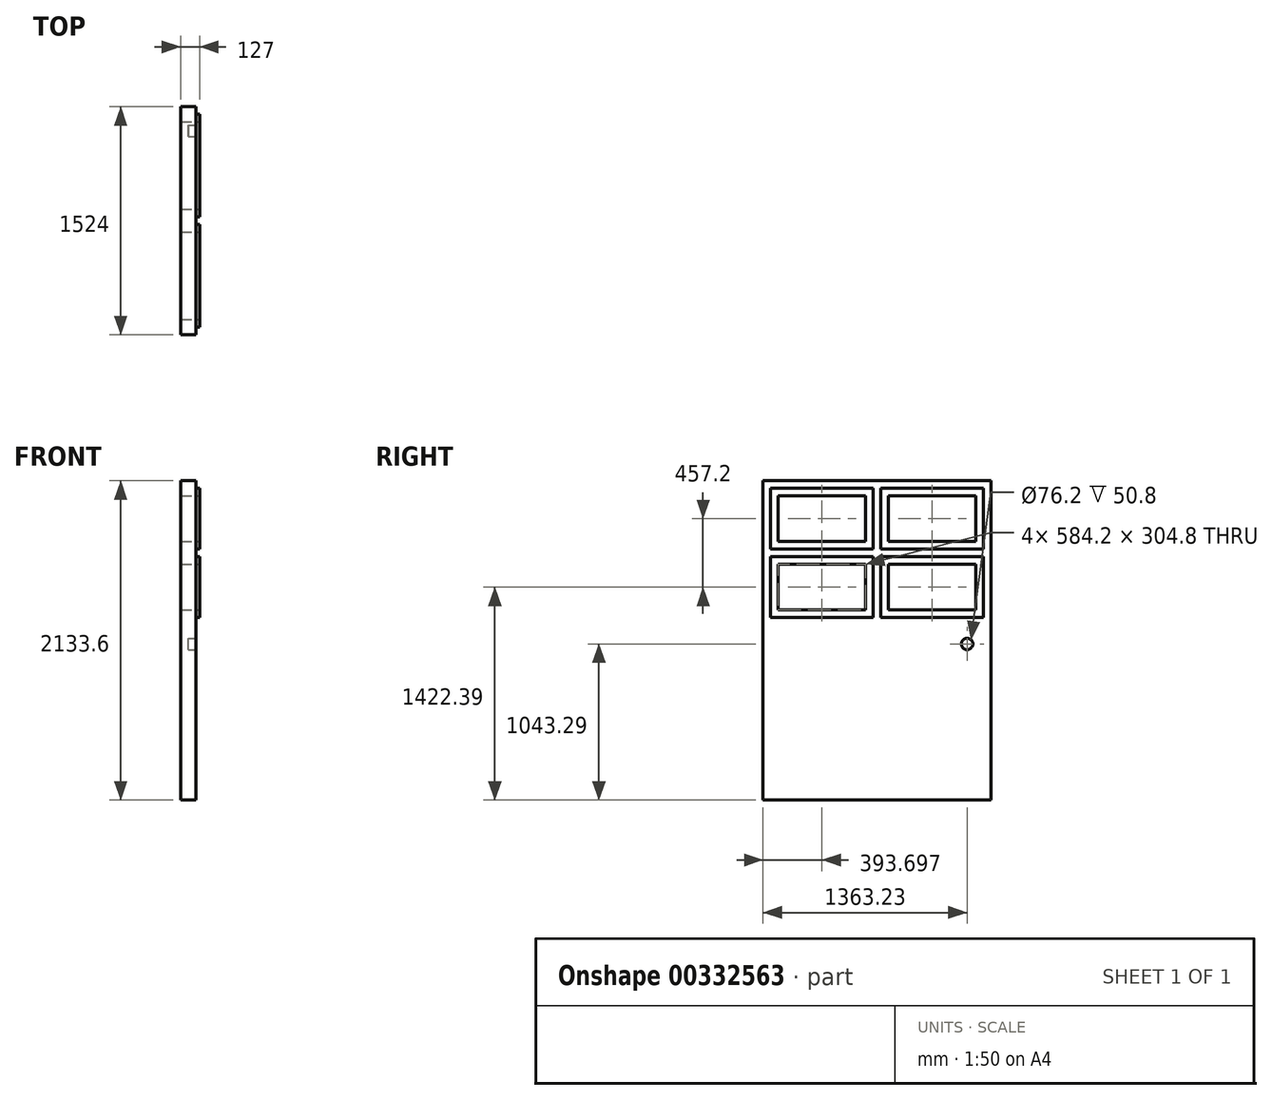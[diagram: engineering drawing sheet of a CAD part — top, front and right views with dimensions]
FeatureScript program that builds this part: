
annotation { "Feature Type Name" : "Feature", "Feature Type Description" : "" }
export const myFeature = defineFeature(function(context is Context, id is Id, definition is map)
    precondition{}
    {
        {
            var Q0;
            Q0=qCreatedBy(makeId("Right.planeOp"),FACE);
            var sketch = newSketch(context, id + "F0", { "sketchPlane" : qUnion([Q0])});
            skLineSegment(sketch, "E0.bottom", {"start": v(-1630.42, -5805.97) * mm, "end": v(-106.42, -5805.97) * mm});
            skLineSegment(sketch, "E0.top", {"start": v(-1630.42, -7939.57) * mm, "end": v(-106.42, -7939.57) * mm});
            skLineSegment(sketch, "E0.left", {"start": v(-1630.42, -5805.97) * mm, "end": v(-1630.42, -7939.57) * mm});
            skLineSegment(sketch, "E0.right", {"start": v(-106.42, -5805.97) * mm, "end": v(-106.42, -7939.57) * mm});
            skSolve(sketch);
        }
        {
            var Q0;
            Q0 = qSketchRegion(id + "F0", true);
            var Q1;
            Q1=makeQuery(id+"F0.imprint","IMPRINT",FACE,{"disambiguationData":[TD([[makeQuery(id+"F0.imprint","IMPRINT",EDGE,{"derivedFrom":sQuery(id+"F0.wireOp",EDGE,"E0.bottom")}),-1.0]])]});
            extrude(context, id + "F1", {"entities" : qUnion([Q0, Q1]), "depth" : 101.6 * mm});
        }
        {
            var Q0;
            Q0=makeQuery(id+"F1.opExtrude","CAP_FACE",FACE,{"disambiguationData":[OSD([sQuery(id+"F0.wireOp",EDGE,"E0.bottom"),sQuery(id+"F0.wireOp",EDGE,"E0.top"),sQuery(id+"F0.wireOp",EDGE,"E0.left"),sQuery(id+"F0.wireOp",EDGE,"E0.right")])],"isStart":false});
            var sketch = newSketch(context, id + "F2", { "sketchPlane" : qUnion([Q0])});
            skCircle(sketch, "E1", {"center": v(-267.2, -6896.28) * mm, "radius": 38.1 * mm});
            skLineSegment(sketch, "E2", {"start": v(-1528.82, -5907.57) * mm, "end": v(-1528.82, -6212.37) * mm});
            skLineSegment(sketch, "E3", {"start": v(-1528.82, -6212.37) * mm, "end": v(-944.62, -6212.37) * mm});
            skLineSegment(sketch, "E4", {"start": v(-208.02, -6212.37) * mm, "end": v(-208.02, -5907.57) * mm});
            skLineSegment(sketch, "E5", {"start": v(-208.02, -5907.57) * mm, "end": v(-792.22, -5907.57) * mm});
            skLineSegment(sketch, "E6", {"start": v(-944.62, -5907.57) * mm, "end": v(-944.62, -6212.37) * mm});
            skPoint(sketch, "E6.endSnap0", {"position": v(-868.42, -6212.37) * mm});
            skLineSegment(sketch, "E7", {"start": v(-792.22, -5907.57) * mm, "end": v(-792.22, -6212.37) * mm});
            skLineSegment(sketch, "E8.trimOffspring", {"start": v(-944.62, -5907.57) * mm, "end": v(-1528.82, -5907.57) * mm});
            skLineSegment(sketch, "E9.trimOffspring", {"start": v(-792.22, -6212.37) * mm, "end": v(-208.02, -6212.37) * mm});
            skLineSegment(sketch, "E10.bottom", {"start": v(-1528.82, -6364.77) * mm, "end": v(-944.62, -6364.77) * mm});
            skLineSegment(sketch, "E10.top", {"start": v(-1528.82, -6669.57) * mm, "end": v(-944.62, -6669.57) * mm});
            skLineSegment(sketch, "E10.left", {"start": v(-1528.82, -6364.77) * mm, "end": v(-1528.82, -6669.57) * mm});
            skLineSegment(sketch, "E10.right", {"start": v(-944.62, -6364.77) * mm, "end": v(-944.62, -6669.57) * mm});
            skLineSegment(sketch, "E11.bottom", {"start": v(-792.22, -6364.77) * mm, "end": v(-208.02, -6364.77) * mm});
            skLineSegment(sketch, "E11.top", {"start": v(-792.22, -6669.57) * mm, "end": v(-208.02, -6669.57) * mm});
            skLineSegment(sketch, "E11.left", {"start": v(-792.22, -6364.77) * mm, "end": v(-792.22, -6669.57) * mm});
            skLineSegment(sketch, "E11.right", {"start": v(-208.02, -6364.77) * mm, "end": v(-208.02, -6669.57) * mm});
            skLineSegment(sketch, "E12.0", {"start": v(-893.82, -5856.77) * mm, "end": v(-1579.62, -5856.77) * mm});
            skLineSegment(sketch, "E12.1", {"start": v(-893.82, -5856.77) * mm, "end": v(-893.82, -6263.17) * mm});
            skLineSegment(sketch, "E12.2", {"start": v(-1579.62, -6263.17) * mm, "end": v(-893.82, -6263.17) * mm});
            skLineSegment(sketch, "E12.3", {"start": v(-1579.62, -5856.77) * mm, "end": v(-1579.62, -6263.17) * mm});
            skLineSegment(sketch, "E13.0", {"start": v(-843.02, -5856.77) * mm, "end": v(-843.02, -6263.17) * mm});
            skLineSegment(sketch, "E13.1", {"start": v(-157.22, -5856.77) * mm, "end": v(-843.02, -5856.77) * mm});
            skLineSegment(sketch, "E13.2", {"start": v(-157.22, -6263.17) * mm, "end": v(-157.22, -5856.77) * mm});
            skLineSegment(sketch, "E13.3", {"start": v(-843.02, -6263.17) * mm, "end": v(-157.22, -6263.17) * mm});
            skLineSegment(sketch, "E14.0", {"start": v(-1579.62, -6313.97) * mm, "end": v(-1579.62, -6720.37) * mm});
            skLineSegment(sketch, "E14.1", {"start": v(-1579.62, -6313.97) * mm, "end": v(-893.82, -6313.97) * mm});
            skLineSegment(sketch, "E14.2", {"start": v(-893.82, -6313.97) * mm, "end": v(-893.82, -6720.37) * mm});
            skLineSegment(sketch, "E14.3", {"start": v(-1579.62, -6720.37) * mm, "end": v(-893.82, -6720.37) * mm});
            skLineSegment(sketch, "E15.0", {"start": v(-843.02, -6313.97) * mm, "end": v(-843.02, -6720.37) * mm});
            skLineSegment(sketch, "E15.1", {"start": v(-843.02, -6313.97) * mm, "end": v(-157.22, -6313.97) * mm});
            skLineSegment(sketch, "E15.2", {"start": v(-157.22, -6313.97) * mm, "end": v(-157.22, -6720.37) * mm});
            skLineSegment(sketch, "E15.3", {"start": v(-843.02, -6720.37) * mm, "end": v(-157.22, -6720.37) * mm});
            skLineSegment(sketch, "E16.bottom", {"start": v(-893.82, -6720.37) * mm, "end": v(-843.02, -6720.37) * mm});
            skLineSegment(sketch, "E16.top", {"start": v(-893.82, -7837.97) * mm, "end": v(-843.02, -7837.97) * mm});
            skLineSegment(sketch, "E16.left", {"start": v(-893.82, -6720.37) * mm, "end": v(-893.82, -7787.17) * mm});
            skLineSegment(sketch, "E16.right", {"start": v(-843.02, -6720.37) * mm, "end": v(-843.02, -7787.17) * mm});
            skLineSegment(sketch, "E17.bottom", {"start": v(-1579.62, -6720.37) * mm, "end": v(-1528.82, -6720.37) * mm});
            skLineSegment(sketch, "E17.top", {"start": v(-1579.62, -7837.97) * mm, "end": v(-1528.82, -7837.97) * mm});
            skLineSegment(sketch, "E17.left", {"start": v(-1579.62, -6720.37) * mm, "end": v(-1579.62, -7837.97) * mm});
            skLineSegment(sketch, "E17.right", {"start": v(-1528.82, -6720.37) * mm, "end": v(-1528.82, -7787.17) * mm});
            skLineSegment(sketch, "E18.bottom", {"start": v(-157.22, -6720.37) * mm, "end": v(-208.02, -6720.37) * mm});
            skLineSegment(sketch, "E18.top", {"start": v(-157.22, -7837.97) * mm, "end": v(-208.02, -7837.97) * mm});
            skLineSegment(sketch, "E18.left", {"start": v(-157.22, -6720.37) * mm, "end": v(-157.22, -7837.97) * mm});
            skLineSegment(sketch, "E18.right", {"start": v(-208.02, -6720.37) * mm, "end": v(-208.02, -7787.17) * mm});
            skLineSegment(sketch, "E19.bottom", {"start": v(-1528.82, -7837.97) * mm, "end": v(-893.82, -7837.97) * mm});
            skLineSegment(sketch, "E19.top", {"start": v(-1528.82, -7787.17) * mm, "end": v(-893.82, -7787.17) * mm});
            skLineSegment(sketch, "E20.bottom", {"start": v(-843.02, -7837.97) * mm, "end": v(-208.02, -7837.97) * mm});
            skLineSegment(sketch, "E20.top", {"start": v(-843.02, -7787.17) * mm, "end": v(-208.02, -7787.17) * mm});
            skSolve(sketch);
        }
        {
            var Q0;
            Q0=makeQuery(id+"F2.imprint","IMPRINT",FACE,{"disambiguationData":[TD([[makeQuery(id+"F2.imprint","IMPRINT",EDGE,{"derivedFrom":sQuery(id+"F2.wireOp",EDGE,"E1")}),1.0]])]});
            extrude(context, id + "F3", {"entities" : qUnion([Q0]), "operationType" : NewBodyOperationType.REMOVE, "oppositeDirection" : true, "depth" : 50.8 * mm});
        }
        {
            var Q0;
            Q0=makeQuery(id+"F2.imprint","IMPRINT",FACE,{"disambiguationData":[TD([[makeQuery(id+"F2.imprint","IMPRINT",EDGE,{"derivedFrom":sQuery(id+"F2.wireOp",EDGE,"E4")}),1.0]])]});
            var Q1;
            Q1=makeQuery(id+"F2.imprint","IMPRINT",FACE,{"disambiguationData":[TD([[makeQuery(id+"F2.imprint","IMPRINT",EDGE,{"derivedFrom":sQuery(id+"F2.wireOp",EDGE,"E2")}),1.0]])]});
            var Q2;
            Q2=makeQuery(id+"F2.imprint","IMPRINT",FACE,{"disambiguationData":[TD([[makeQuery(id+"F2.imprint","IMPRINT",EDGE,{"derivedFrom":sQuery(id+"F2.wireOp",EDGE,"E10.bottom")}),-1.0]])]});
            var Q3;
            Q3=makeQuery(id+"F2.imprint","IMPRINT",FACE,{"disambiguationData":[TD([[makeQuery(id+"F2.imprint","IMPRINT",EDGE,{"derivedFrom":sQuery(id+"F2.wireOp",EDGE,"E11.bottom")}),-1.0]])]});
            extrude(context, id + "F4", {"entities" : qUnion([Q0, Q1, Q2, Q3]), "operationType" : NewBodyOperationType.REMOVE, "endBound" : BoundingType.THROUGH_ALL, "oppositeDirection" : true, "depth" : 25.4 * mm});
        }
        {
            var Q0;
            Q0=makeQuery(id+"F2.imprint","IMPRINT",FACE,{"disambiguationData":[TD([[makeQuery(id+"F2.imprint","IMPRINT",EDGE,{"derivedFrom":sQuery(id+"F2.wireOp",EDGE,"E10.bottom")}),1.0]])]});
            var Q1;
            Q1=makeQuery(id+"F2.imprint","IMPRINT",FACE,{"disambiguationData":[TD([[makeQuery(id+"F2.imprint","IMPRINT",EDGE,{"derivedFrom":sQuery(id+"F2.wireOp",EDGE,"E2")}),-1.0]])]});
            var Q2;
            Q2=makeQuery(id+"F2.imprint","IMPRINT",FACE,{"disambiguationData":[TD([[makeQuery(id+"F2.imprint","IMPRINT",EDGE,{"derivedFrom":sQuery(id+"F2.wireOp",EDGE,"E11.bottom")}),1.0]])]});
            var Q3;
            Q3=makeQuery(id+"F2.imprint","IMPRINT",FACE,{"disambiguationData":[TD([[makeQuery(id+"F2.imprint","IMPRINT",EDGE,{"derivedFrom":sQuery(id+"F2.wireOp",EDGE,"E4")}),-1.0]])]});
            extrude(context, id + "F5", {"entities" : qUnion([Q0, Q1, Q2, Q3]), "operationType" : NewBodyOperationType.ADD, "depth" : 25.4 * mm});
        }
    });
